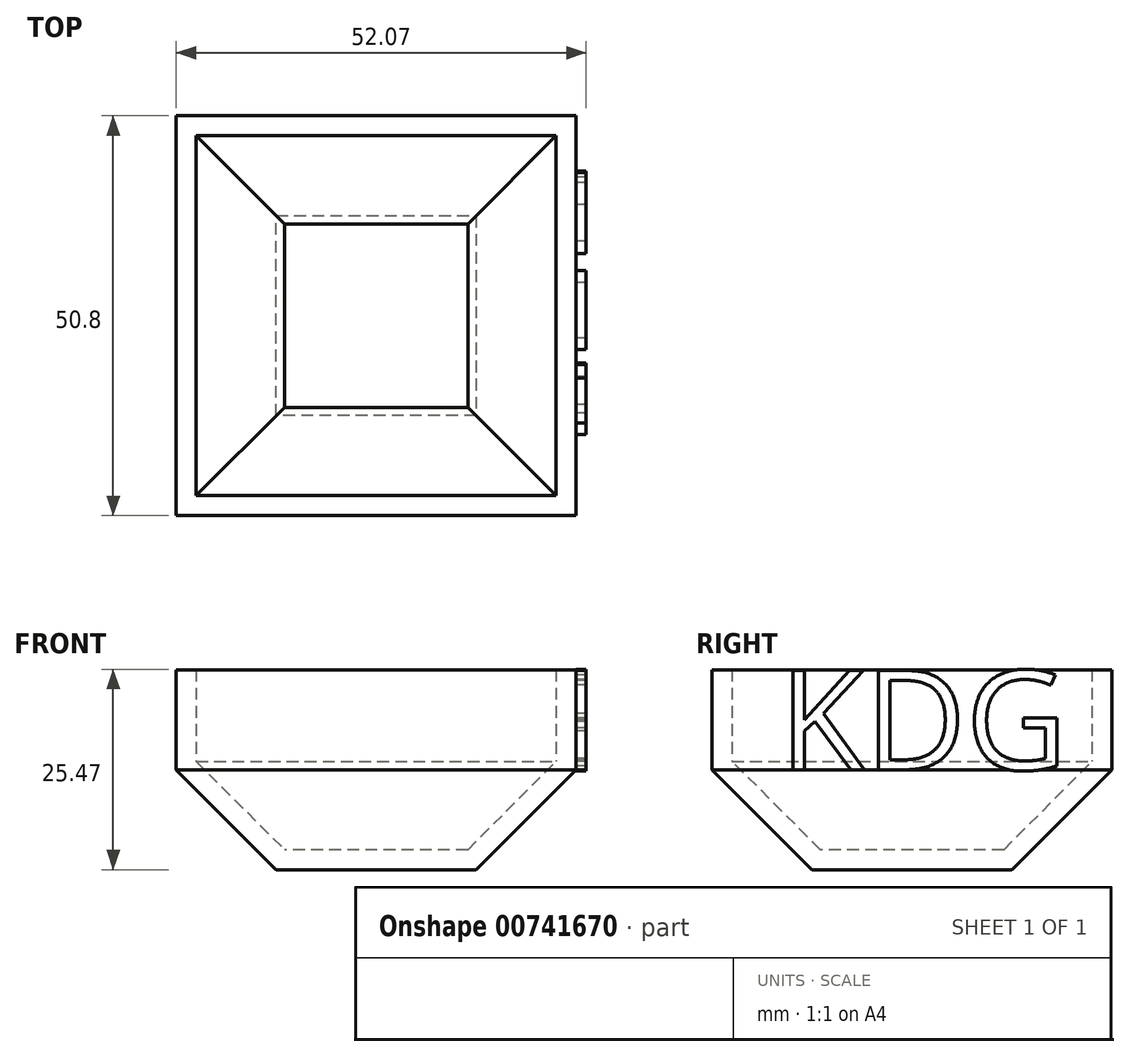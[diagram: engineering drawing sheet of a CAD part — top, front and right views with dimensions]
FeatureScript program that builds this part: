
annotation { "Feature Type Name" : "Feature", "Feature Type Description" : "" }
export const myFeature = defineFeature(function(context is Context, id is Id, definition is map)
    precondition{}
    {
        {
            var Q0;
            Q0=qCreatedBy(makeId("Front.planeOp"),FACE);
            var sketch = newSketch(context, id + "F0", { "sketchPlane" : qUnion([Q0])});
            skLineSegment(sketch, "E0", {"start": v(-69.16, 32.88) * mm, "end": v(-18.36, 32.88) * mm});
            skLineSegment(sketch, "E1", {"start": v(-69.16, 32.88) * mm, "end": v(-69.16, 7.48) * mm});
            skLineSegment(sketch, "E2", {"start": v(-69.16, 7.48) * mm, "end": v(-18.36, 7.48) * mm});
            skLineSegment(sketch, "E3", {"start": v(-18.36, 32.88) * mm, "end": v(-18.36, 7.48) * mm});
            skSolve(sketch);
        }
        {
            var Q0;
            Q0=makeQuery(id+"F0.imprint","IMPRINT",FACE,{"disambiguationData":[TD([[makeQuery(id+"F0.imprint","IMPRINT",EDGE,{"derivedFrom":sQuery(id+"F0.wireOp",EDGE,"E0")}),-1.0]])]});
            extrude(context, id + "F1", {"entities" : qUnion([Q0]), "depth" : 50.8 * mm, "offsetDistance" : 25.4 * mm});
        }
        {
            var Q0;
            Q0=makeQuery(id+"F1.opExtrude","SWEPT_FACE",FACE,{"disambiguationData":[OSD([sQuery(id+"F0.wireOp",EDGE,"E2")])]});
            chamfer(context, id + "F2", {"entities" : qUnion([Q0]), "width" : 12.7 * mm, "tangentPropagation" : true});
        }
        {
            var Q0;
            Q0=makeQuery(id+"F1.opExtrude","SWEPT_FACE",FACE,{"disambiguationData":[OSD([sQuery(id+"F0.wireOp",EDGE,"E0")])]});
            shell(context, id + "F3", {"entities" : qUnion([Q0]), "thickness" : 2.54 * mm});
        }
        {
            var Q0;
            Q0=makeQuery(id+"F1.opExtrude","SWEPT_FACE",FACE,{"disambiguationData":[OSD([sQuery(id+"F0.wireOp",EDGE,"E3")])]});
            var sketch = newSketch(context, id + "F4", { "sketchPlane" : qUnion([Q0])});
            skText(sketch, "E4", { "text": "KDG", "fontName": "OpenSans-Regular.ttf"});
            const initialGuessF4  = {"E4": [-0.04224, 0.02018, 1, 0, 0.0127]};
            skSetInitialGuess(sketch, initialGuessF4);
            skSolve(sketch);
        }
        {
            var Q0;
            Q0 = qSketchRegion(id + "F4", true);
            extrude(context, id + "F5", {"entities" : qUnion([Q0]), "operationType" : NewBodyOperationType.ADD, "depth" : 1.27 * mm, "offsetDistance" : 25.4 * mm});
        }
    });
